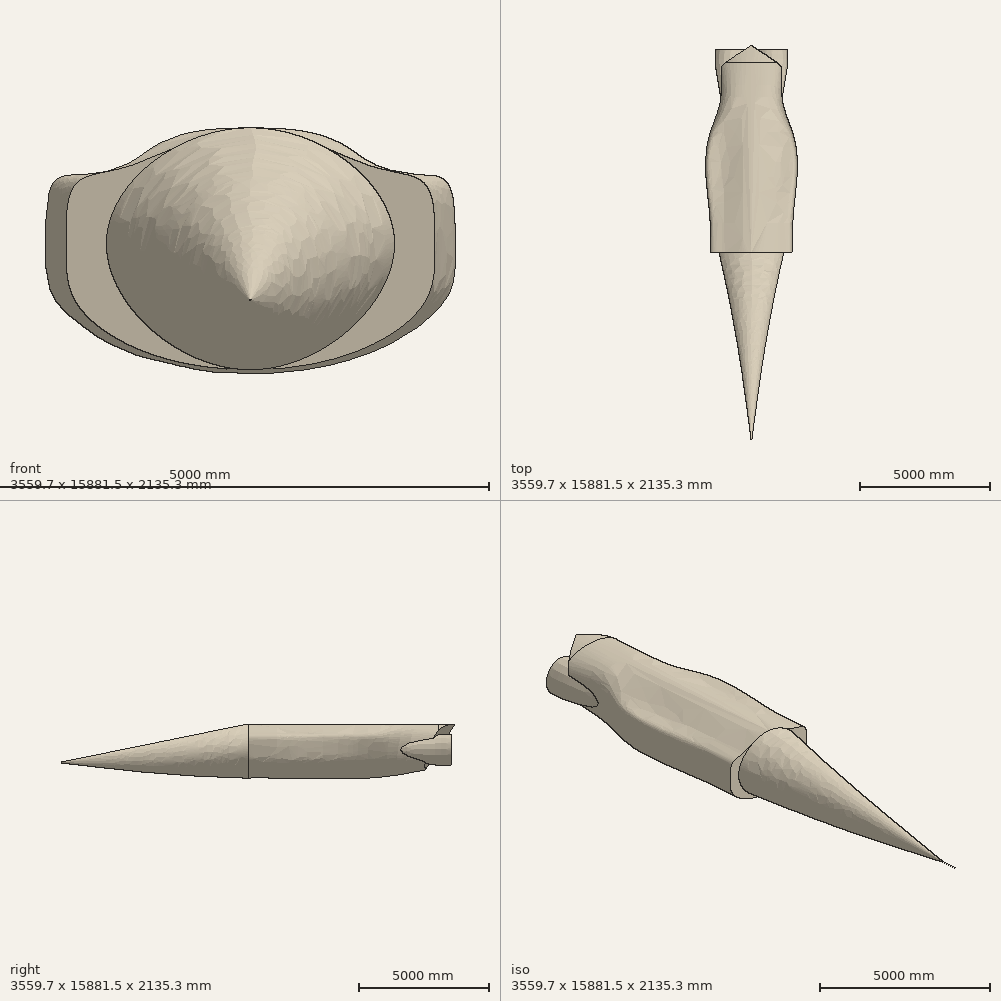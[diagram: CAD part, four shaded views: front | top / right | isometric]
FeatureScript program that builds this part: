
annotation { "Feature Type Name" : "Feature", "Feature Type Description" : "" }
export const myFeature = defineFeature(function(context is Context, id is Id, definition is map)
    precondition{}
    {
        {
            var Q0;
            Q0=qCreatedBy(makeId("Right.planeOp"),FACE);
            var sketch = newSketch(context, id + "F0", { "sketchPlane" : qUnion([Q0])});
            skLineSegment(sketch, "E0", {"start": v(0, 0) * mm, "end": v(-1750, 0) * mm});
            skLineSegment(sketch, "E1", {"start": v(-1750, 0) * mm, "end": v(-3500, 0) * mm});
            skLineSegment(sketch, "E2", {"start": v(-3500, 0) * mm, "end": v(-3500, -1000) * mm});
            skLineSegment(sketch, "E3", {"start": v(-3500, -1000) * mm, "end": v(-8500, -1000) * mm});
            skLineSegment(sketch, "E4", {"start": v(-8500, -1000) * mm, "end": v(-8500, -499.31) * mm});
            skLineSegment(sketch, "E5", {"start": v(-1151.4, 0) * mm, "end": v(-1151.4, 1000) * mm});
            skLineSegment(sketch, "E6", {"start": v(-1151.4, 1000) * mm, "end": v(-8500, -499.31) * mm});
            skLineSegment(sketch, "E7", {"start": v(-8500, -499.31) * mm, "end": v(-3500, -1000) * mm});
            skLineSegment(sketch, "E8", {"start": v(-3500, 0) * mm, "end": v(-3500, 520.82) * mm});
            skLineSegment(sketch, "E9", {"start": v(-8500, -499.31) * mm, "end": v(-8450, -499.31) * mm});
            skLineSegment(sketch, "E10", {"start": v(-8450, -499.31) * mm, "end": v(-8450, -489.1) * mm});
            skLineSegment(sketch, "E11", {"start": v(-8450, -499.31) * mm, "end": v(-8450, -504.32) * mm});
            skSolve(sketch);
        }
        {
            var Q0;
            Q0=sQuery(id+"F0.wireOp",EDGE,"E5");
            cPlane(context, id + "F1", {"entities" : qUnion([Q0]), "cplaneType" : CPlaneType.LINE_ANGLE, "offset" : 25 * mm, "angle" : 90 * degree, "oppositeDirection" : true, "width" : 150 * mm, "height" : 150 * mm});
        }
        {
            var Q0;
            Q0=qCreatedBy(id+"F1.planeOp",FACE);
            var sketch = newSketch(context, id + "F2", { "sketchPlane" : qUnion([Q0])});
            skPoint(sketch, "E12.middle", {"position": v(0, 0) * mm});
            skFitSpline(sketch, "E13", {"points": [v(0, 1000) * mm, v(-1060, 662.5) * mm, v(-1517.6, 506.84) * mm, v(-1600, 0) * mm, v(-1517.6, -506.84) * mm, v(-750, -1000) * mm, v(750, -1000) * mm, v(1517.6, -506.84) * mm, v(1600, 0) * mm, v(1517.6, 506.84) * mm, v(1060, 662.5) * mm, v(0, 1000) * mm]});
            skSolve(sketch);
        }
        {
            var Q0;
            Q0=qCreatedBy(makeId("Front.planeOp"),FACE);
            var sketch = newSketch(context, id + "F3", { "sketchPlane" : qUnion([Q0])});
            skPoint(sketch, "E14.middle", {"position": v(0, 0) * mm});
            skFitSpline(sketch, "E15", {"points": [v(0, 1000) * mm, v(-1060, 662.5) * mm, v(-1517.6, 506.84) * mm, v(-1600, 0) * mm, v(-1517.6, -506.84) * mm, v(-750, -1000) * mm, v(750, -1000) * mm, v(1517.6, -506.84) * mm, v(1600, 0) * mm, v(1517.6, 506.84) * mm, v(1060, 662.5) * mm, v(0, 1000) * mm]});
            skSolve(sketch);
        }
        {
            var Q0;
            Q0=qCreatedBy(makeId("Front.planeOp"),FACE);
            cPlane(context, id + "F4", {"entities" : qUnion([Q0]), "cplaneType" : CPlaneType.OFFSET, "offset" : 3500 * mm, "oppositeDirection" : true, "width" : 150 * mm, "height" : 150 * mm});
        }
        {
            var Q0;
            Q0=qCreatedBy(id+"F4.planeOp",FACE);
            var sketch = newSketch(context, id + "F5", { "sketchPlane" : qUnion([Q0])});
            skPoint(sketch, "E16.middle", {"position": v(0, 0) * mm});
            skFitSpline(sketch, "E17", {"points": [v(0, 1000) * mm, v(-1060, 662.5) * mm, v(-1517.6, 506.84) * mm, v(-1600, 0) * mm, v(-1517.6, -506.84) * mm, v(-750, -1000) * mm, v(750, -1000) * mm, v(1517.6, -506.84) * mm, v(1600, 0) * mm, v(1517.6, 506.84) * mm, v(1060, 662.5) * mm, v(0, 1000) * mm]});
            skSolve(sketch);
        }
        {
            var Q0;
            Q0=qCreatedBy(makeId("Front.planeOp"),FACE);
            cPlane(context, id + "F6", {"entities" : qUnion([Q0]), "cplaneType" : CPlaneType.OFFSET, "offset" : 4500 * mm, "oppositeDirection" : true, "width" : 150 * mm, "height" : 150 * mm});
        }
        {
            var Q0;
            Q0=qCreatedBy(id+"F6.planeOp",FACE);
            var sketch = newSketch(context, id + "F7", { "sketchPlane" : qUnion([Q0])});
            skPoint(sketch, "E18.middle", {"position": v(0, 0) * mm});
            skFitSpline(sketch, "E19", {"points": [v(0, 1000) * mm, v(-1060, 662.5) * mm, v(-1250, 0) * mm, v(-1060, -662.5) * mm, v(0, -1000) * mm, v(1060, -662.5) * mm, v(1250, 0) * mm, v(1060, 662.5) * mm, v(0, 1000) * mm]});
            skSolve(sketch);
        }
        {
            var Q0;
            Q0=qCreatedBy(makeId("Front.planeOp"),FACE);
            cPlane(context, id + "F8", {"entities" : qUnion([Q0]), "cplaneType" : CPlaneType.OFFSET, "offset" : 6232.05 * mm, "oppositeDirection" : true, "width" : 150 * mm, "height" : 150 * mm});
        }
        {
            var Q0;
            Q0=qCreatedBy(id+"F8.planeOp",FACE);
            var sketch = newSketch(context, id + "F9", { "sketchPlane" : qUnion([Q0])});
            skPoint(sketch, "E20.middle", {"position": v(0, 0) * mm});
            skFitSpline(sketch, "E21", {"points": [v(0, 1000) * mm, v(-1060, 662.5) * mm, v(-1250, 0) * mm, v(-848, -530) * mm, v(848, -530) * mm, v(1250, 0) * mm, v(1060, 662.5) * mm, v(0, 1000) * mm]});
            skSolve(sketch);
        }
        {
            var Q0;
            Q0=makeQuery(id+"F2.imprint","IMPRINT",FACE,{"disambiguationData":[TD([[makeQuery(id+"F2.imprint","IMPRINT",EDGE,{"derivedFrom":sQuery(id+"F2.wireOp",EDGE,"E13")}),1.0]])]});
            var Q1;
            Q1=makeQuery(id+"F3.imprint","IMPRINT",FACE,{"disambiguationData":[TD([[makeQuery(id+"F3.imprint","IMPRINT",EDGE,{"derivedFrom":sQuery(id+"F3.wireOp",EDGE,"E15")}),1.0]])]});
            var Q2;
            Q2=makeQuery(id+"F5.imprint","IMPRINT",FACE,{"disambiguationData":[TD([[makeQuery(id+"F5.imprint","IMPRINT",EDGE,{"derivedFrom":sQuery(id+"F5.wireOp",EDGE,"E17")}),1.0]])]});
            var Q3;
            Q3=makeQuery(id+"F7.imprint","IMPRINT",FACE,{"disambiguationData":[TD([[makeQuery(id+"F7.imprint","IMPRINT",EDGE,{"derivedFrom":sQuery(id+"F7.wireOp",EDGE,"E19")}),1.0]])]});
            var Q4;
            Q4=makeQuery(id+"F9.imprint","IMPRINT",FACE,{"disambiguationData":[TD([[makeQuery(id+"F9.imprint","IMPRINT",EDGE,{"derivedFrom":sQuery(id+"F9.wireOp",EDGE,"E21")}),1.0]])]});
            loft(context, id + "F10", {"sheetProfilesArray" : [{ "sheetProfileEntities" : qUnion([Q0]) }, { "sheetProfileEntities" : qUnion([Q1]) }, { "sheetProfileEntities" : qUnion([Q2]) }, { "sheetProfileEntities" : qUnion([Q3]) }, { "sheetProfileEntities" : qUnion([Q4]) }]});
        }
        {
            var Q0;
            Q0=makeQuery(id+"F10.opLoft","CAP_FACE",FACE,{"disambiguationData":[OSD([makeQuery(id+"F9.imprint","IMPRINT",FACE,{"disambiguationData":[TD([[makeQuery(id+"F9.imprint","IMPRINT",EDGE,{"derivedFrom":sQuery(id+"F9.wireOp",EDGE,"E21")}),1.0]])]})])],"isStart":true});
            extrude(context, id + "F11", {"entities" : qUnion([Q0]), "operationType" : NewBodyOperationType.ADD, "depth" : 649.4 * mm, "offsetDistance" : 25 * mm});
        }
        {
            var Q0;
            Q0=qCreatedBy(makeId("Right.planeOp"),FACE);
            var sketch = newSketch(context, id + "F12", { "sketchPlane" : qUnion([Q0])});
            skLineSegment(sketch, "E22", {"start": v(0, 0) * mm, "end": v(4500, 0) * mm});
            skLineSegment(sketch, "E23", {"start": v(4500, 0) * mm, "end": v(6232.05, 0) * mm});
            skLineSegment(sketch, "E24", {"start": v(4500, 0) * mm, "end": v(4500, 1000) * mm});
            skLineSegment(sketch, "E25", {"start": v(4500, 1000) * mm, "end": v(6881.46, 1000) * mm});
            skLineSegment(sketch, "E26", {"start": v(6881.46, 1000) * mm, "end": v(6881.46, -1000) * mm});
            skLineSegment(sketch, "E27", {"start": v(6881.46, 1000) * mm, "end": v(6232.05, 0) * mm});
            skLineSegment(sketch, "E28", {"start": v(6232.05, 0) * mm, "end": v(5582.64, -1000) * mm});
            skLineSegment(sketch, "E29", {"start": v(5582.64, -1000) * mm, "end": v(6881.46, -1000) * mm});
            skSolve(sketch);
        }
        {
            var Q0;
            Q0=makeQuery(id+"F12.imprint","IMPRINT",FACE,{"disambiguationData":[TD([[makeQuery(id+"F12.imprint","IMPRINT",EDGE,{"derivedFrom":sQuery(id+"F12.wireOp",EDGE,"E26")}),-1.0]])]});
            var Q1;
            Q1=sQuery(id+"F12.wireOp",EDGE,"E25");
            revolve(context, id + "F13", {"operationType" : NewBodyOperationType.REMOVE, "entities" : qUnion([Q0]), "axis" : qUnion([Q1]), "revolveType" : RevolveType.SYMMETRIC, "oppositeDirection" : true, "angle" : 182 * degree});
        }
        {
            var Q0;
            Q0=qCreatedBy(id+"F1.planeOp",FACE);
            var sketch = newSketch(context, id + "F14", { "sketchPlane" : qUnion([Q0])});
            skFitSpline(sketch, "E30", {"points": [v(0, 1000) * mm, v(-1250, 0) * mm, v(0, -1099.92) * mm, v(1250, 0) * mm, v(0, 1000) * mm]});
            skSolve(sketch);
        }
        {
            var Q0;
            Q0=qCreatedBy(makeId("Front.planeOp"),FACE);
            cPlane(context, id + "F15", {"entities" : qUnion([Q0]), "cplaneType" : CPlaneType.OFFSET, "offset" : 3500 * mm, "width" : 150 * mm, "height" : 150 * mm});
        }
        {
            var Q0;
            Q0=qCreatedBy(id+"F15.planeOp",FACE);
            var sketch = newSketch(context, id + "F16", { "sketchPlane" : qUnion([Q0])});
            skCircle(sketch, "E31", {"center": v(0, -239.59) * mm, "radius": 760.41 * mm});
            skSolve(sketch);
        }
        {
            var Q0;
            Q0=qCreatedBy(makeId("Front.planeOp"),FACE);
            cPlane(context, id + "F17", {"entities" : qUnion([Q0]), "cplaneType" : CPlaneType.OFFSET, "offset" : 8450 * mm, "width" : 150 * mm, "height" : 150 * mm});
        }
        {
            var Q0;
            Q0=qCreatedBy(id+"F17.planeOp",FACE);
            var sketch = newSketch(context, id + "F18", { "sketchPlane" : qUnion([Q0])});
            skCircle(sketch, "E32", {"center": v(0, -496.71) * mm, "radius": 7.6 * mm});
            skSolve(sketch);
        }
        {
            var Q1;
            Q1=makeQuery(id+"F18.imprint","IMPRINT",FACE,{"disambiguationData":[TD([[makeQuery(id+"F18.imprint","IMPRINT",EDGE,{"derivedFrom":sQuery(id+"F18.wireOp",EDGE,"E32")}),1.0]])]});
            var Q2;
            Q2=makeQuery(id+"F16.imprint","IMPRINT",FACE,{"disambiguationData":[TD([[makeQuery(id+"F16.imprint","IMPRINT",EDGE,{"derivedFrom":sQuery(id+"F16.wireOp",EDGE,"E31")}),1.0]])]});
            var Q3;
            Q3=makeQuery(id+"F14.imprint","IMPRINT",FACE,{"disambiguationData":[TD([[makeQuery(id+"F14.imprint","IMPRINT",EDGE,{"derivedFrom":sQuery(id+"F14.wireOp",EDGE,"E30")}),1.0]])]});
            loft(context, id + "F19", {"operationType" : NewBodyOperationType.ADD, "sheetProfilesArray" : [{ "sheetProfileEntities" : qUnion([Q1]) }, { "sheetProfileEntities" : qUnion([Q2]) }, { "sheetProfileEntities" : qUnion([Q3]) }]});
        }
        {
            var Q0;
            Q0=makeQuery(id+"F19.opLoft","CAP_FACE",FACE,{"disambiguationData":[OSD([makeQuery(id+"F18.imprint","IMPRINT",FACE,{"disambiguationData":[TD([[makeQuery(id+"F18.imprint","IMPRINT",EDGE,{"derivedFrom":sQuery(id+"F18.wireOp",EDGE,"E32")}),1.0]])]})])],"isStart":true});
            extrude(context, id + "F20", {"entities" : qUnion([Q0]), "operationType" : NewBodyOperationType.ADD, "depth" : 550 * mm, "offsetDistance" : 25 * mm});
        }
        {
            var Q0;
            Q0=qCreatedBy(makeId("Front.planeOp"),FACE);
            cPlane(context, id + "F21", {"entities" : qUnion([Q0]), "cplaneType" : CPlaneType.OFFSET, "offset" : 3500 * mm, "oppositeDirection" : true, "width" : 150 * mm, "height" : 150 * mm});
        }
        {
            var Q0;
            Q0=qCreatedBy(id+"F21.planeOp",FACE);
            var sketch = newSketch(context, id + "F22", { "sketchPlane" : qUnion([Q0])});
            skCircle(sketch, "E33", {"center": v(-800, 0) * mm, "radius": 600 * mm});
            skCircle(sketch, "E34", {"center": v(800, 0) * mm, "radius": 600 * mm});
            skSolve(sketch);
        }
        {
            var Q0;
            Q0=qCreatedBy(makeId("Front.planeOp"),FACE);
            cPlane(context, id + "F23", {"entities" : qUnion([Q0]), "cplaneType" : CPlaneType.OFFSET, "offset" : 4500 * mm, "oppositeDirection" : true, "width" : 150 * mm, "height" : 150 * mm});
        }
        {
            var Q0;
            Q0=qCreatedBy(id+"F23.planeOp",FACE);
            var sketch = newSketch(context, id + "F24", { "sketchPlane" : qUnion([Q0])});
            skCircle(sketch, "E35", {"center": v(-800, 0) * mm, "radius": 400 * mm});
            skCircle(sketch, "E36", {"center": v(800, 0) * mm, "radius": 400 * mm});
            skSolve(sketch);
        }
        {
            var Q0;
            Q0=qCreatedBy(makeId("Front.planeOp"),FACE);
            cPlane(context, id + "F25", {"entities" : qUnion([Q0]), "cplaneType" : CPlaneType.OFFSET, "offset" : 6232.05 * mm, "oppositeDirection" : true, "width" : 150 * mm, "height" : 150 * mm});
        }
        {
            var Q0;
            Q0=qCreatedBy(id+"F25.planeOp",FACE);
            var sketch = newSketch(context, id + "F26", { "sketchPlane" : qUnion([Q0])});
            skCircle(sketch, "E37", {"center": v(-800, 0) * mm, "radius": 600 * mm});
            skCircle(sketch, "E38", {"center": v(800, 0) * mm, "radius": 600 * mm});
            skSolve(sketch);
        }
        {
            var Q0;
            Q0=qCreatedBy(makeId("Front.planeOp"),FACE);
            cPlane(context, id + "F27", {"entities" : qUnion([Q0]), "cplaneType" : CPlaneType.OFFSET, "offset" : 6732.05 * mm, "oppositeDirection" : true, "width" : 150 * mm, "height" : 150 * mm});
        }
        {
            var Q0;
            Q0=qCreatedBy(id+"F27.planeOp",FACE);
            var sketch = newSketch(context, id + "F28", { "sketchPlane" : qUnion([Q0])});
            skCircle(sketch, "E39", {"center": v(-800, 0) * mm, "radius": 600 * mm});
            skCircle(sketch, "E40", {"center": v(800, 0) * mm, "radius": 600 * mm});
            skSolve(sketch);
        }
        {
            var Q0;
            Q0=makeQuery(id+"F22.imprint","IMPRINT",FACE,{"disambiguationData":[TD([[makeQuery(id+"F22.imprint","IMPRINT",EDGE,{"derivedFrom":sQuery(id+"F22.wireOp",EDGE,"E33")}),1.0]])]});
            var Q1;
            Q1=makeQuery(id+"F24.imprint","IMPRINT",FACE,{"disambiguationData":[TD([[makeQuery(id+"F24.imprint","IMPRINT",EDGE,{"derivedFrom":sQuery(id+"F24.wireOp",EDGE,"E35")}),1.0]])]});
            var Q2;
            Q2=makeQuery(id+"F26.imprint","IMPRINT",FACE,{"disambiguationData":[TD([[makeQuery(id+"F26.imprint","IMPRINT",EDGE,{"derivedFrom":sQuery(id+"F26.wireOp",EDGE,"E37")}),1.0]])]});
            var Q3;
            Q3=makeQuery(id+"F28.imprint","IMPRINT",FACE,{"disambiguationData":[TD([[makeQuery(id+"F28.imprint","IMPRINT",EDGE,{"derivedFrom":sQuery(id+"F28.wireOp",EDGE,"E39")}),1.0]])]});
            loft(context, id + "F29", {"sheetProfilesArray" : [{ "sheetProfileEntities" : qUnion([Q0]) }, { "sheetProfileEntities" : qUnion([Q1]) }, { "sheetProfileEntities" : qUnion([Q2]) }, { "sheetProfileEntities" : qUnion([Q3]) }]});
        }
        {
            var Q0;
            Q0=makeQuery(id+"F22.imprint","IMPRINT",FACE,{"disambiguationData":[TD([[makeQuery(id+"F22.imprint","IMPRINT",EDGE,{"derivedFrom":sQuery(id+"F22.wireOp",EDGE,"E34")}),1.0]])]});
            var Q1;
            Q1=makeQuery(id+"F24.imprint","IMPRINT",FACE,{"disambiguationData":[TD([[makeQuery(id+"F24.imprint","IMPRINT",EDGE,{"derivedFrom":sQuery(id+"F24.wireOp",EDGE,"E36")}),1.0]])]});
            var Q2;
            Q2=makeQuery(id+"F26.imprint","IMPRINT",FACE,{"disambiguationData":[TD([[makeQuery(id+"F26.imprint","IMPRINT",EDGE,{"derivedFrom":sQuery(id+"F26.wireOp",EDGE,"E38")}),1.0]])]});
            var Q3;
            Q3=makeQuery(id+"F28.imprint","IMPRINT",FACE,{"disambiguationData":[TD([[makeQuery(id+"F28.imprint","IMPRINT",EDGE,{"derivedFrom":sQuery(id+"F28.wireOp",EDGE,"E40")}),1.0]])]});
            loft(context, id + "F30", {"sheetProfilesArray" : [{ "sheetProfileEntities" : qUnion([Q0]) }, { "sheetProfileEntities" : qUnion([Q1]) }, { "sheetProfileEntities" : qUnion([Q2]) }, { "sheetProfileEntities" : qUnion([Q3]) }]});
        }
        {
            var Q0;
            Q0=qCreatedBy(makeId("Right.planeOp"),FACE);
            cPlane(context, id + "F31", {"entities" : qUnion([Q0]), "cplaneType" : CPlaneType.OFFSET, "offset" : 1250 * mm, "oppositeDirection" : true, "width" : 150 * mm, "height" : 150 * mm});
        }
        {
            var Q0;
            Q0=qCreatedBy(makeId("Right.planeOp"),FACE);
            cPlane(context, id + "F32", {"entities" : qUnion([Q0]), "cplaneType" : CPlaneType.OFFSET, "offset" : 1250 * mm, "width" : 150 * mm, "height" : 150 * mm});
        }
    });
